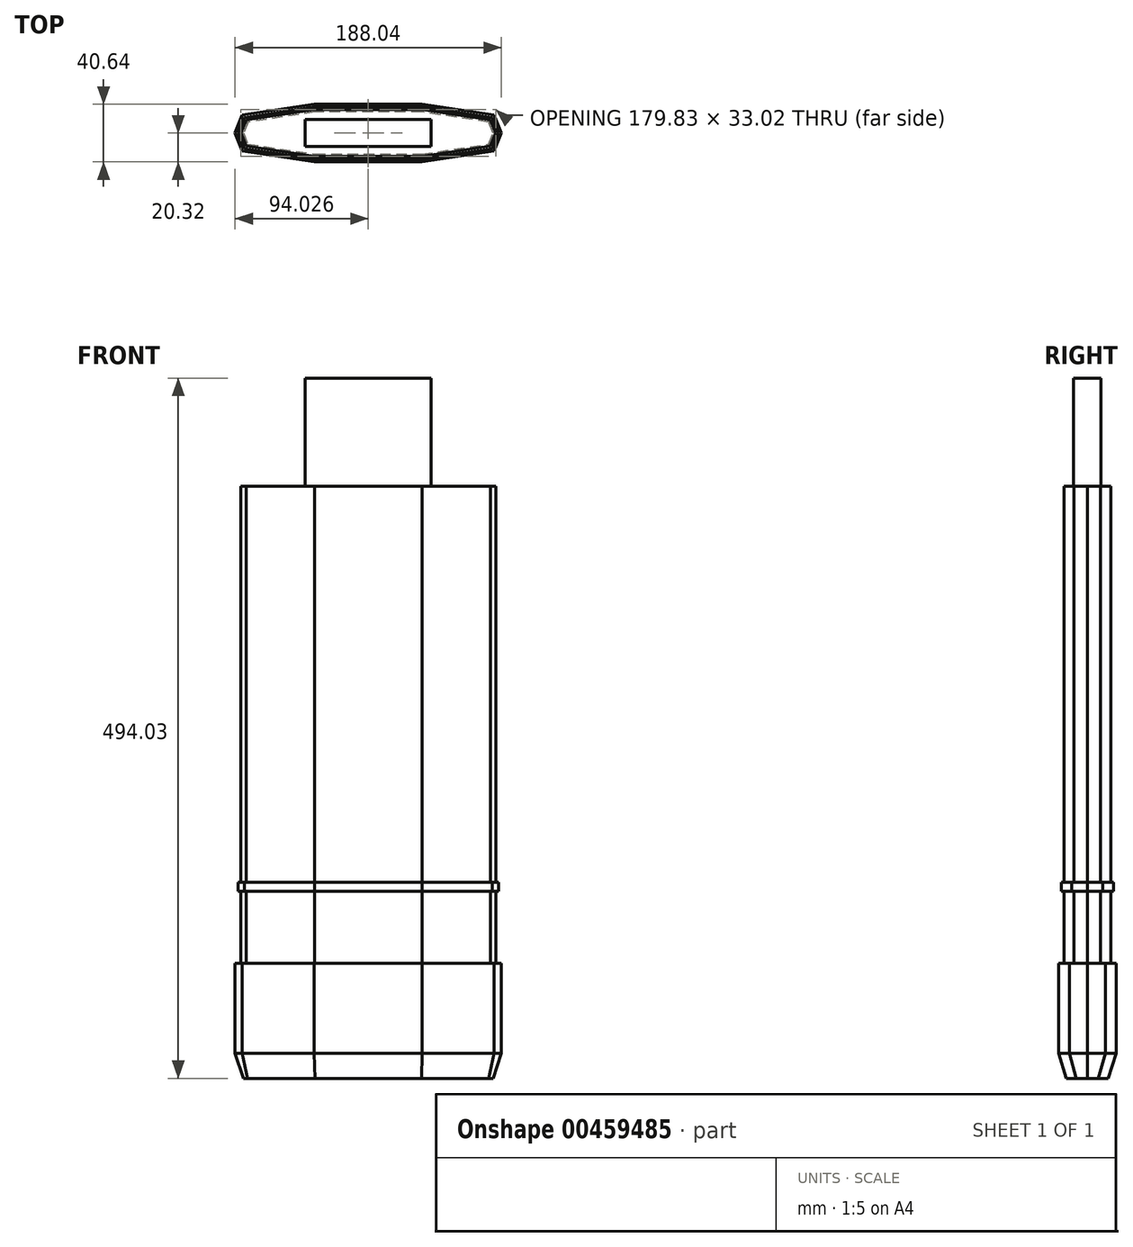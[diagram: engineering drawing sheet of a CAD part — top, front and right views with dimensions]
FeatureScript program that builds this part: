
annotation { "Feature Type Name" : "Feature", "Feature Type Description" : "" }
export const myFeature = defineFeature(function(context is Context, id is Id, definition is map)
    precondition{}
    {
        {
            var Q0;
            Q0=qCreatedBy(makeId("Top.planeOp"),FACE);
            var sketch = newSketch(context, id + "F0", { "sketchPlane" : qUnion([Q0])});
            skLineSegment(sketch, "E0", {"start": v(-108.35, 12.7) * mm, "end": v(-57.55, 20.32) * mm});
            skLineSegment(sketch, "E1", {"start": v(-57.55, 20.32) * mm, "end": v(18.65, 20.32) * mm});
            skLineSegment(sketch, "E2", {"start": v(18.65, 20.32) * mm, "end": v(69.45, 12.7) * mm});
            skLineSegment(sketch, "E3", {"start": v(69.45, -12.7) * mm, "end": v(18.65, -20.32) * mm});
            skLineSegment(sketch, "E4", {"start": v(18.65, -20.32) * mm, "end": v(-57.55, -20.32) * mm});
            skLineSegment(sketch, "E5", {"start": v(-57.55, -20.32) * mm, "end": v(-108.43, -12.7) * mm});
            skLineSegment(sketch, "E6", {"start": v(-108.35, 12.7) * mm, "end": v(-113.5, 0) * mm});
            skLineSegment(sketch, "E7", {"start": v(-113.5, 0) * mm, "end": v(-108.43, -12.7) * mm});
            skLineSegment(sketch, "E8", {"start": v(69.45, 12.7) * mm, "end": v(74.53, 0) * mm});
            skLineSegment(sketch, "E9", {"start": v(69.45, -12.7) * mm, "end": v(74.53, 0) * mm});
            skSolve(sketch);
        }
        {
            var Q0;
            Q0=makeQuery(id+"F0.imprint","IMPRINT",FACE,{"disambiguationData":[TD([[makeQuery(id+"F0.imprint","IMPRINT",EDGE,{"derivedFrom":sQuery(id+"F0.wireOp",EDGE,"E0")}),-1.0]])]});
            extrude(context, id + "F1", {"entities" : qUnion([Q0]), "depth" : 63.5 * mm});
        }
        {
            var Q0;
            Q0=makeQuery(id+"F1.opExtrude","CAP_FACE",FACE,{"disambiguationData":[OSD([sQuery(id+"F0.wireOp",EDGE,"E0"),sQuery(id+"F0.wireOp",EDGE,"E1"),sQuery(id+"F0.wireOp",EDGE,"E2"),sQuery(id+"F0.wireOp",EDGE,"E3"),sQuery(id+"F0.wireOp",EDGE,"E4"),sQuery(id+"F0.wireOp",EDGE,"E5"),sQuery(id+"F0.wireOp",EDGE,"E6"),sQuery(id+"F0.wireOp",EDGE,"E7"),sQuery(id+"F0.wireOp",EDGE,"E8"),sQuery(id+"F0.wireOp",EDGE,"E9")])],"isStart":false});
            var sketch = newSketch(context, id + "F2", { "sketchPlane" : qUnion([Q0])});
            skSolve(sketch);
        }
        {
            var Q0;
            Q0=makeQuery(id+"F1.opExtrude","CAP_FACE",FACE,{"disambiguationData":[OSD([sQuery(id+"F0.wireOp",EDGE,"E0"),sQuery(id+"F0.wireOp",EDGE,"E1"),sQuery(id+"F0.wireOp",EDGE,"E2"),sQuery(id+"F0.wireOp",EDGE,"E3"),sQuery(id+"F0.wireOp",EDGE,"E4"),sQuery(id+"F0.wireOp",EDGE,"E5"),sQuery(id+"F0.wireOp",EDGE,"E6"),sQuery(id+"F0.wireOp",EDGE,"E7"),sQuery(id+"F0.wireOp",EDGE,"E8"),sQuery(id+"F0.wireOp",EDGE,"E9")])],"isStart":true});
            var sketch = newSketch(context, id + "F3", { "sketchPlane" : qUnion([Q0])});
            skLineSegment(sketch, "E10.0", {"start": v(18.08, 12.7) * mm, "end": v(-56.98, 12.7) * mm});
            skLineSegment(sketch, "E10.1", {"start": v(64, 5.81) * mm, "end": v(18.08, 12.7) * mm});
            skLineSegment(sketch, "E10.2", {"start": v(-56.98, 12.7) * mm, "end": v(-102.97, 5.81) * mm});
            skLineSegment(sketch, "E10.3", {"start": v(66.33, 0) * mm, "end": v(64, 5.81) * mm});
            skLineSegment(sketch, "E10.4", {"start": v(64, -5.81) * mm, "end": v(66.33, 0) * mm});
            skLineSegment(sketch, "E10.5", {"start": v(18.08, -12.7) * mm, "end": v(64, -5.81) * mm});
            skLineSegment(sketch, "E10.6", {"start": v(-102.97, 5.81) * mm, "end": v(-105.3, 0.02) * mm});
            skLineSegment(sketch, "E10.7", {"start": v(-105.3, 0.02) * mm, "end": v(-102.92, -5.8) * mm});
            skLineSegment(sketch, "E10.8", {"start": v(-102.92, -5.8) * mm, "end": v(-56.98, -12.7) * mm});
            skLineSegment(sketch, "E10.9", {"start": v(-56.98, -12.7) * mm, "end": v(18.08, -12.7) * mm});
            skSolve(sketch);
        }
        {
            var Q0;
            Q0=makeQuery(id+"F3.imprint","IMPRINT",FACE,{"disambiguationData":[TD([[makeQuery(id+"F3.imprint","IMPRINT",EDGE,{"derivedFrom":sQuery(id+"F3.wireOp",EDGE,"E10.0")}),-1.0]])]});
            var Q1;
            Q1=makeQuery(id+"F3.imprint","IMPRINT",FACE,{"disambiguationData":[TD([[makeQuery(id+"F3.imprint","IMPRINT",EDGE,{"derivedFrom":sQuery(id+"F3.wireOp",EDGE,"E10.0")}),1.0]])]});
            extrude(context, id + "F4", {"entities" : qUnion([Q0, Q1]), "operationType" : NewBodyOperationType.ADD, "depth" : 17.78 * mm, "hasDraft" : true, "draftAngle" : 17 * degree, "draftPullDirection" : true});
        }
        {
            var Q0;
            Q0=makeQuery(id+"F2.imprint","IMPRINT",FACE,{"disambiguationData":[TD([[makeQuery(id+"F2.imprint","IMPRINT",EDGE,{"derivedFrom":makeQuery(id+"F1.opExtrude","CAP_EDGE",EDGE,{"disambiguationData":[OSD([sQuery(id+"F0.wireOp",EDGE,"E0")])],"isStart":false})}),-1.0]])]});
            var sketch = newSketch(context, id + "F5", { "sketchPlane" : qUnion([Q0])});
            skLineSegment(sketch, "E11.0", {"start": v(-109.4, -0.01) * mm, "end": v(-105.7, -9.26) * mm});
            skLineSegment(sketch, "E11.1", {"start": v(-105.63, 9.25) * mm, "end": v(-109.4, -0.01) * mm});
            skLineSegment(sketch, "E11.2", {"start": v(-105.7, -9.26) * mm, "end": v(-57.26, -16.51) * mm});
            skLineSegment(sketch, "E11.3", {"start": v(-57.26, 16.5) * mm, "end": v(-105.63, 9.25) * mm});
            skLineSegment(sketch, "E11.4", {"start": v(18.37, 16.5) * mm, "end": v(-57.26, 16.5) * mm});
            skLineSegment(sketch, "E11.5", {"start": v(66.73, 9.26) * mm, "end": v(18.37, 16.5) * mm});
            skLineSegment(sketch, "E11.6", {"start": v(-57.26, -16.51) * mm, "end": v(18.37, -16.5) * mm});
            skLineSegment(sketch, "E11.7", {"start": v(18.37, -16.5) * mm, "end": v(66.73, -9.26) * mm});
            skLineSegment(sketch, "E11.8", {"start": v(66.73, -9.26) * mm, "end": v(70.43, 0) * mm});
            skLineSegment(sketch, "E11.9", {"start": v(70.43, 0) * mm, "end": v(66.73, 9.26) * mm});
            skSolve(sketch);
        }
        {
            var Q0;
            Q0 = qSketchRegion(id + "F5", true);
            extrude(context, id + "F6", {"entities" : qUnion([Q0]), "operationType" : NewBodyOperationType.ADD, "depth" : 50.8 * mm});
        }
        {
            var Q0;
            Q0=makeQuery(id+"F6.opExtrude","CAP_FACE",FACE,{"disambiguationData":[OSD([sQuery(id+"F5.wireOp",EDGE,"E11.0"),sQuery(id+"F5.wireOp",EDGE,"E11.1"),sQuery(id+"F5.wireOp",EDGE,"E11.2"),sQuery(id+"F5.wireOp",EDGE,"E11.3"),sQuery(id+"F5.wireOp",EDGE,"E11.4"),sQuery(id+"F5.wireOp",EDGE,"E11.5"),sQuery(id+"F5.wireOp",EDGE,"E11.6"),sQuery(id+"F5.wireOp",EDGE,"E11.7"),sQuery(id+"F5.wireOp",EDGE,"E11.8"),sQuery(id+"F5.wireOp",EDGE,"E11.9")])],"isStart":false});
            var sketch = newSketch(context, id + "F7", { "sketchPlane" : qUnion([Q0])});
            skLineSegment(sketch, "E12.0", {"start": v(18.51, -18.41) * mm, "end": v(68.1, -10.98) * mm});
            skLineSegment(sketch, "E12.1", {"start": v(-57.4, -18.41) * mm, "end": v(18.51, -18.41) * mm});
            skLineSegment(sketch, "E12.2", {"start": v(68.1, -10.98) * mm, "end": v(72.48, 0) * mm});
            skLineSegment(sketch, "E12.3", {"start": v(-107.06, -10.98) * mm, "end": v(-57.4, -18.42) * mm});
            skLineSegment(sketch, "E12.4", {"start": v(-111.45, 0) * mm, "end": v(-107.06, -10.98) * mm});
            skLineSegment(sketch, "E12.5", {"start": v(-107, 10.98) * mm, "end": v(-111.45, 0) * mm});
            skLineSegment(sketch, "E12.6", {"start": v(72.48, 0) * mm, "end": v(68.1, 10.98) * mm});
            skLineSegment(sketch, "E12.7", {"start": v(68.1, 10.98) * mm, "end": v(18.51, 18.41) * mm});
            skLineSegment(sketch, "E12.8", {"start": v(18.51, 18.41) * mm, "end": v(-57.4, 18.41) * mm});
            skLineSegment(sketch, "E12.9", {"start": v(-57.4, 18.41) * mm, "end": v(-107, 10.98) * mm});
            skSolve(sketch);
        }
        {
            var Q0;
            Q0 = qSketchRegion(id + "F7", true);
            extrude(context, id + "F8", {"entities" : qUnion([Q0]), "operationType" : NewBodyOperationType.ADD, "depth" : 6.35 * mm});
        }
        {
            var Q0;
            Q0=makeQuery(id+"F8.opExtrude","CAP_FACE",FACE,{"disambiguationData":[OSD([sQuery(id+"F7.wireOp",EDGE,"E12.0"),sQuery(id+"F7.wireOp",EDGE,"E12.1"),sQuery(id+"F7.wireOp",EDGE,"E12.2"),sQuery(id+"F7.wireOp",EDGE,"E12.3"),sQuery(id+"F7.wireOp",EDGE,"E12.4"),sQuery(id+"F7.wireOp",EDGE,"E12.5"),sQuery(id+"F7.wireOp",EDGE,"E12.6"),sQuery(id+"F7.wireOp",EDGE,"E12.7"),sQuery(id+"F7.wireOp",EDGE,"E12.8"),sQuery(id+"F7.wireOp",EDGE,"E12.9")])],"isStart":false});
            var sketch = newSketch(context, id + "F9", { "sketchPlane" : qUnion([Q0])});
            skLineSegment(sketch, "E13.0", {"start": v(66.73, 9.26) * mm, "end": v(18.37, 16.5) * mm});
            skLineSegment(sketch, "E13.1", {"start": v(70.43, 0) * mm, "end": v(66.73, 9.26) * mm});
            skLineSegment(sketch, "E13.2", {"start": v(18.37, 16.5) * mm, "end": v(-57.26, 16.5) * mm});
            skLineSegment(sketch, "E13.3", {"start": v(66.73, -9.26) * mm, "end": v(70.43, 0) * mm});
            skLineSegment(sketch, "E13.4", {"start": v(18.37, -16.5) * mm, "end": v(66.73, -9.26) * mm});
            skLineSegment(sketch, "E13.5", {"start": v(-57.26, -16.51) * mm, "end": v(18.37, -16.5) * mm});
            skLineSegment(sketch, "E13.6", {"start": v(-57.26, 16.5) * mm, "end": v(-105.63, 9.25) * mm});
            skLineSegment(sketch, "E13.7", {"start": v(-105.63, 9.25) * mm, "end": v(-109.4, -0.01) * mm});
            skLineSegment(sketch, "E13.8", {"start": v(-109.4, -0.01) * mm, "end": v(-105.7, -9.26) * mm});
            skLineSegment(sketch, "E13.9", {"start": v(-105.7, -9.26) * mm, "end": v(-57.26, -16.51) * mm});
            skSolve(sketch);
        }
        {
            var Q0;
            Q0=makeQuery(id+"F9.imprint","IMPRINT",FACE,{"disambiguationData":[TD([[makeQuery(id+"F9.imprint","IMPRINT",EDGE,{"derivedFrom":sQuery(id+"F9.wireOp",EDGE,"E13.0")}),1.0]])]});
            extrude(context, id + "F10", {"entities" : qUnion([Q0]), "operationType" : NewBodyOperationType.ADD, "depth" : 279.4 * mm});
        }
        {
            var Q0;
            Q0=makeQuery(id+"F10.opExtrude","CAP_FACE",FACE,{"disambiguationData":[OSD([sQuery(id+"F9.wireOp",EDGE,"E13.0"),sQuery(id+"F9.wireOp",EDGE,"E13.1"),sQuery(id+"F9.wireOp",EDGE,"E13.2"),sQuery(id+"F9.wireOp",EDGE,"E13.3"),sQuery(id+"F9.wireOp",EDGE,"E13.4"),sQuery(id+"F9.wireOp",EDGE,"E13.5"),sQuery(id+"F9.wireOp",EDGE,"E13.6"),sQuery(id+"F9.wireOp",EDGE,"E13.7"),sQuery(id+"F9.wireOp",EDGE,"E13.8"),sQuery(id+"F9.wireOp",EDGE,"E13.9")])],"isStart":false});
            var sketch = newSketch(context, id + "F11", { "sketchPlane" : qUnion([Q0])});
            skLineSegment(sketch, "E14", {"start": v(-63.9, 9.51) * mm, "end": v(25, 9.51) * mm});
            skLineSegment(sketch, "E15", {"start": v(25, 9.51) * mm, "end": v(25, -9.54) * mm});
            skLineSegment(sketch, "E16", {"start": v(25, -9.54) * mm, "end": v(-63.9, -9.54) * mm});
            skLineSegment(sketch, "E17", {"start": v(-63.9, -9.54) * mm, "end": v(-63.9, 9.51) * mm});
            skSolve(sketch);
        }
        {
            var Q0;
            Q0=makeQuery(id+"F11.imprint","IMPRINT",FACE,{"disambiguationData":[TD([[makeQuery(id+"F11.imprint","IMPRINT",EDGE,{"derivedFrom":sQuery(id+"F11.wireOp",EDGE,"E14")}),-1.0]])]});
            extrude(context, id + "F12", {"entities" : qUnion([Q0]), "operationType" : NewBodyOperationType.ADD, "depth" : 76.2 * mm});
        }
    });
